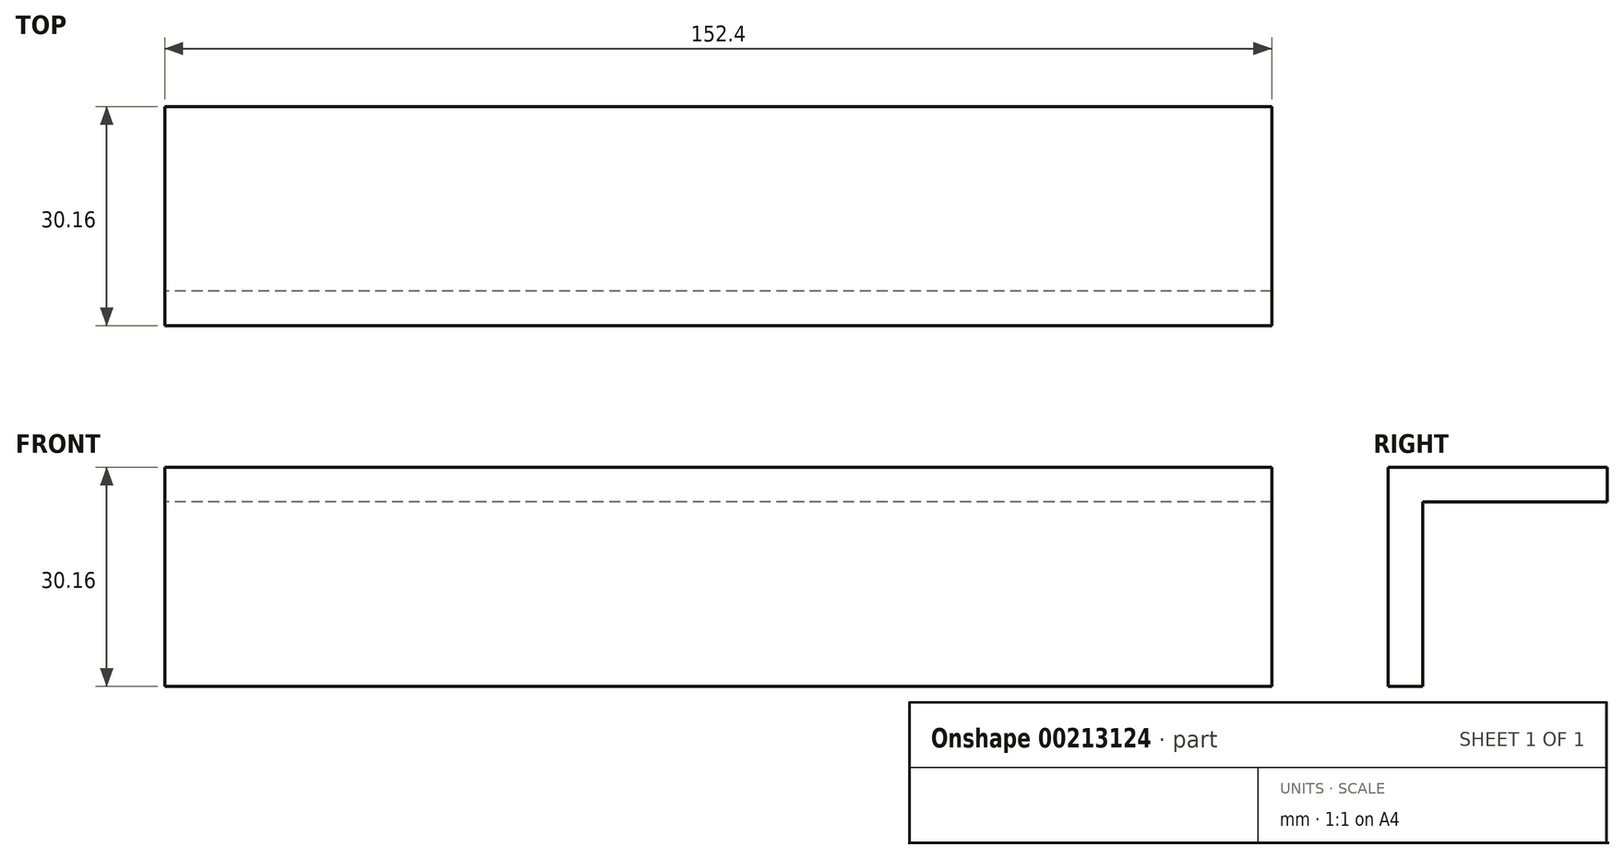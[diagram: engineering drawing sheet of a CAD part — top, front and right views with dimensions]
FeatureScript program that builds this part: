
annotation { "Feature Type Name" : "Feature", "Feature Type Description" : "" }
export const myFeature = defineFeature(function(context is Context, id is Id, definition is map)
    precondition{}
    {
        {
            var Q0;
            Q0=qCreatedBy(makeId("Right.planeOp"),FACE);
            var sketch = newSketch(context, id + "F0", { "sketchPlane" : qUnion([Q0])});
            skLineSegment(sketch, "E0.bottom", {"start": v(-12.7, 12.7) * mm, "end": v(12.7, 12.7) * mm});
            skLineSegment(sketch, "E0.left", {"start": v(-12.7, 12.7) * mm, "end": v(-12.7, -12.7) * mm});
            skPoint(sketch, "E0.middle", {"position": v(0, 0) * mm});
            skLineSegment(sketch, "E1.0", {"start": v(-17.46, 17.46) * mm, "end": v(-17.46, -12.7) * mm});
            skLineSegment(sketch, "E1.1", {"start": v(-17.46, 17.46) * mm, "end": v(12.7, 17.46) * mm});
            skLineSegment(sketch, "E2", {"start": v(-17.46, -12.7) * mm, "end": v(-12.7, -12.7) * mm});
            skLineSegment(sketch, "E3", {"start": v(12.7, 12.7) * mm, "end": v(12.7, 17.46) * mm});
            skPoint(sketch, "E0.top.end.orphan", {"position": v(12.7, -12.7) * mm});
            skSolve(sketch);
        }
        {
            var Q0;
            Q0 = qSketchRegion(id + "F0", true);
            extrude(context, id + "F1", {"entities" : qUnion([Q0]), "endBound" : BoundingType.SYMMETRIC, "depth" : 152.4 * mm});
        }
    });
